# Revit family: IS_Idealrain_B9506_BIM_DE
name_source: partatom
category: Plumbing Fixtures
revit_build: Autodesk Revit MEP 2016 (Build: 20161004_0715(x64)
units: mm (PartAtom-declared; Revit-internal decimal feet)

## family parameters
Cut with Voids When Loaded = No
Host = Face
OmniClass Number = 23.45.05.14.17
OmniClass Title = Showers
Part Type = Normal
Room Calculation Point = No
Round Connector Dimension = Use Diameter
Shared = No

## types (1)
- B9506AA - IDEALRAIN S1 SPRCH.SADA 1F/80
    Accessories = www.idealstandard.de\ersatzteile
    AreaUnits = millimeters
    Assembly Code = C1030200
    AssetType = Fixed
    BIMObjectName = ISI_IdealStandard_Showers_IDEALRAIN_B9506AA
    BarCode = 3800861023944
    Brand = Ideal Standard
    CodePerformance = 0
    Color = Chrome
    ConnectionType = Mechanical
    Cost = 0 $
    CurrencyUnit = €
    Default Elevation = 0 mm  [stored 0 ft]
    Description = IDEALRAIN S1 SPRCH.SADA 1F/80
    DurationUnit = year
    ExpectedLife = 25
    Features = IDEALRAIN shower set with single function 80mm handspray
    Finish = Chrome
    GrossWeight = 0,656 kg
    InstallationDate = 1900-12-31T23:59:59
    InstallationInstructions = www.idealstandard.de\produkte
    LinearUnits = millimeters
    ManufacturerURL = www.idealstandard.de
    Material = Brass
    Model = B9506AA
    ModelNumber = B9506AA
    ModelReference = IS Handbrause-Set IDEALRAIN 1-Funktionshandbrause, d:80mm Chrom
    Name = ISI_IdealStandard_Showers_IDEALRAIN_B9506AA
    NominalDepth = 0 mm  [stored 0 ft]
    NominalHeight = 238 mm
    NominalLength = 149 mm
    NominalWidth = 110 mm
    ProductInformation = www.idealstandard.de
    Shape = Sculptured
    Size = 240 x 150 x 110 mm
    Space = Internal
    URL = www.idealstandard.de
    Uniclass2015Code = Pr_40_20_87_75
    Uniclass2015Title = Shower fittings package
    Uniclass2015Version = Products v1.1
    Version = 1
    VolumeUnits = Litres

note: [stored X ft] marks values corroborated as IEEE doubles in the binary element streams (Revit-internal decimal feet)

## geometry (parser evidence)
native form markers: Blend x4, Sweep x1
no freeform markers — native parametric forms only
